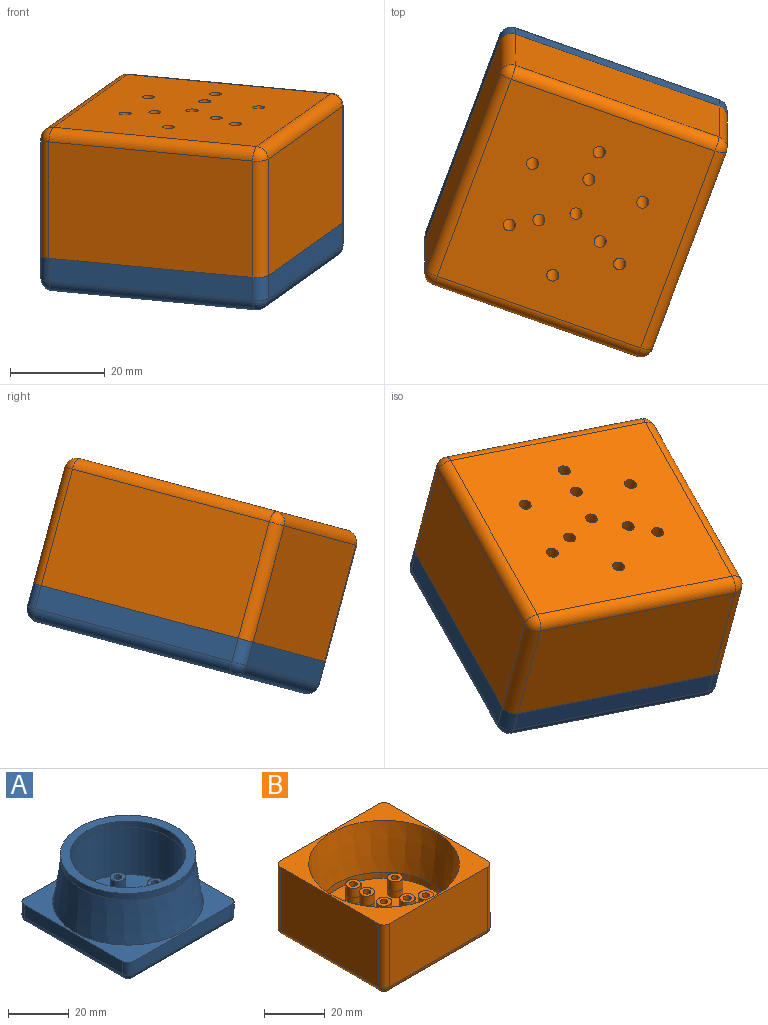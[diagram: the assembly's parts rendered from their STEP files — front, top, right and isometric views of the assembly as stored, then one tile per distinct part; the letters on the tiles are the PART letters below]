
ASSEMBLY  parts=2 mates=1
PART A: 52 faces, bbox 50.8x50.8x26.7 mm
  f0: plane 45.72x5.08mm, normal (-1,0,0), area 232.3mm2, adj f13,f17,f19,f51
  f1: plane 45.72x5.08mm, normal (0,-1,0), area 232.3mm2, adj f10,f16,f19,f51
  f2: plane 45.72x5.08mm, normal (1,0,0), area 232.3mm2, adj f8,f10,f11,f51
  f3: plane 45.72x5.08mm, normal (0,1,0), area 232.3mm2, adj f8,f12,f13,f51
  f4: plane 45.72x45.72mm, normal (0,0,-1), area 2044.9mm2, adj f11,f12,f16,f17,f38,f39,f40,f41
  f5: plane 38.09x38.09mm, normal (0,0,1), area 956.1mm2, adj f6,f20,f22,f24,f26,f28,f30,f32
  f6: cylinder r=19.04mm len=38.09mm, axis (0,0,-1), area 2279.4mm2, adj f5,f48
  f7: cone r=22.23mm half-angle=7.6deg, axis (0,0,-1), area 2837.1mm2, adj f47,f50
  f8: cylinder r=2.54mm len=5.08mm, axis (0,0,1), area 20.3mm2, adj f2,f3,f9,f51
  f9: sphere r=2.54mm, area 10.1mm2, adj f8,f11,f12
  f10: cylinder r=2.54mm len=5.08mm, axis (0,0,-1), area 20.3mm2, adj f1,f2,f14,f51
  f11: cylinder r=2.54mm len=45.72mm, axis (0,1,0), area 182.4mm2, adj f2,f4,f9,f14
  f12: cylinder r=2.54mm len=45.72mm, axis (-1,0,0), area 182.4mm2, adj f3,f4,f9,f15
  f13: cylinder r=2.54mm len=5.08mm, axis (0,0,1), area 20.3mm2, adj f0,f3,f15,f51
  f14: sphere r=2.54mm, area 10.1mm2, adj f10,f11,f16
  f15: sphere r=2.54mm, area 10.1mm2, adj f12,f13,f17
  f16: cylinder r=2.54mm len=45.72mm, axis (1,0,0), area 182.4mm2, adj f1,f4,f14,f18
  f17: cylinder r=2.54mm len=45.72mm, axis (0,-1,0), area 182.4mm2, adj f0,f4,f15,f18
  f18: sphere r=2.54mm, area 10.1mm2, adj f16,f17,f19
  f19: cylinder r=2.54mm len=5.08mm, axis (0,0,-1), area 20.3mm2, adj f0,f1,f18,f51
  f20: cylinder r=2.55mm len=5.09mm, axis (0,0,-1), area 60.9mm2, adj f5,f21
  f21: plane 5.09x5.09mm, normal (0,0,1), area 15.3mm2, adj f20,f39
  f22: cylinder r=2.55mm len=5.09mm, axis (0,0,-1), area 60.9mm2, adj f5,f23
  f23: plane 5.09x5.09mm, normal (0,0,1), area 15.3mm2, adj f22,f46
  f24: cylinder r=2.55mm len=5.09mm, axis (0,0,-1), area 60.9mm2, adj f5,f25
  f25: plane 5.09x5.09mm, normal (0,0,1), area 15.3mm2, adj f24,f45
  f26: cylinder r=2.55mm len=5.09mm, axis (0,0,-1), area 60.9mm2, adj f5,f27
  f27: plane 5.09x5.09mm, normal (0,0,1), area 15.3mm2, adj f26,f43
  f28: cylinder r=2.55mm len=5.09mm, axis (0,0,-1), area 60.9mm2, adj f5,f29
  f29: plane 5.09x5.09mm, normal (0,0,1), area 15.3mm2, adj f28,f42
  f30: cylinder r=2.55mm len=5.09mm, axis (0,0,-1), area 60.9mm2, adj f5,f31
  f31: plane 5.09x5.09mm, normal (0,0,1), area 15.3mm2, adj f30,f40
  f32: cylinder r=2.55mm len=5.09mm, axis (0,0,-1), area 60.9mm2, adj f5,f33
  f33: plane 5.09x5.09mm, normal (0,0,1), area 15.3mm2, adj f32,f41
  f34: cylinder r=2.55mm len=5.09mm, axis (0,0,-1), area 60.9mm2, adj f5,f35
  f35: plane 5.09x5.09mm, normal (0,0,1), area 15.3mm2, adj f34,f38
  f36: cylinder r=2.55mm len=5.09mm, axis (0,0,-1), area 60.9mm2, adj f5,f37
  f37: plane 5.09x5.09mm, normal (0,0,1), area 15.3mm2, adj f36,f44
  f38: cylinder r=1.27mm len=8.89mm, axis (0,0,1), area 70.9mm2, adj f4,f35
  f39: cylinder r=1.27mm len=8.89mm, axis (0,0,1), area 70.9mm2, adj f4,f21
  f40: cylinder r=1.27mm len=8.89mm, axis (0,0,1), area 70.9mm2, adj f4,f31
  f41: cylinder r=1.27mm len=8.89mm, axis (0,0,1), area 70.9mm2, adj f4,f33
  f42: cylinder r=1.27mm len=8.89mm, axis (0,0,1), area 70.9mm2, adj f4,f29
  f43: cylinder r=1.27mm len=8.89mm, axis (0,0,1), area 70.9mm2, adj f4,f27
  f44: cylinder r=1.27mm len=8.89mm, axis (0,0,1), area 70.9mm2, adj f4,f37
  f45: cylinder r=1.27mm len=8.89mm, axis (0,0,1), area 70.9mm2, adj f4,f25
  f46: cylinder r=1.27mm len=8.89mm, axis (0,0,1), area 70.9mm2, adj f4,f23
  f47: cone r=22.23mm half-angle=1.1deg, axis (0,0,1), area 355.2mm2, adj f7,f49
  f48: cone r=19.04mm half-angle=1.1deg, axis (0,0,-1), area 303.6mm2, adj f6,f49
  f49: plane 44.55x44.55mm, normal (0,0,1), area 425.1mm2, adj f47,f48
  f50: cylinder r=24.77mm len=49.53mm, axis (0,0,-1), area 395.2mm2, adj f7,f51
  f51: plane 50.8x50.8mm, normal (0,0,1), area 648.5mm2, adj f0,f1,f2,f3,f8,f10,f13,f19
PART B: 61 faces, bbox 50.8x50.8x27.9 mm
  f0: plane 45.72x25.4mm, normal (-1,0,0), area 1161.4mm2, adj f4,f49,f50,f51
  f1: plane 45.72x25.4mm, normal (0,-1,0), area 1161.3mm2, adj f4,f49,f54,f55
  f2: plane 45.72x25.4mm, normal (1,0,0), area 1161.4mm2, adj f4,f55,f56,f60
  f3: plane 45.72x25.4mm, normal (0,1,0), area 1161.3mm2, adj f4,f50,f56,f57
  f4: plane 50.8x50.8mm, normal (0,0,1), area 648.6mm2, adj f0,f1,f2,f3,f5,f49,f50,f55
  f5: cone r=22.25mm half-angle=7.5deg, axis (0,0,1), area 2838.1mm2, adj f4,f45
  f6: cylinder r=2.55mm len=5.09mm, axis (0,0,-1), area 60.9mm2, adj f7,f44
  f7: plane 5.09x5.09mm, normal (0,0,1), area 15.3mm2, adj f6,f26
  f8: cylinder r=2.55mm len=5.09mm, axis (0,0,-1), area 60.9mm2, adj f9,f43
  f9: plane 5.09x5.09mm, normal (0,0,1), area 15.3mm2, adj f8,f27
  f10: cylinder r=2.55mm len=5.09mm, axis (0,0,-1), area 60.9mm2, adj f11,f42
  f11: plane 5.09x5.09mm, normal (0,0,1), area 15.3mm2, adj f10,f33
  f12: cylinder r=2.55mm len=5.09mm, axis (0,0,-1), area 60.9mm2, adj f13,f41
  f13: plane 5.09x5.09mm, normal (0,0,1), area 15.3mm2, adj f12,f30
  f14: cylinder r=2.55mm len=5.09mm, axis (0,0,-1), area 60.9mm2, adj f15,f40
  f15: plane 5.09x5.09mm, normal (0,0,1), area 15.3mm2, adj f14,f28
  f16: cylinder r=2.55mm len=5.09mm, axis (0,0,-1), area 60.9mm2, adj f17,f39
  f17: plane 5.09x5.09mm, normal (0,0,1), area 15.3mm2, adj f16,f29
  f18: cylinder r=2.55mm len=5.09mm, axis (0,0,-1), area 60.9mm2, adj f19,f38
  f19: plane 5.09x5.09mm, normal (0,0,1), area 15.3mm2, adj f18,f31
  f20: cylinder r=2.55mm len=5.09mm, axis (0,0,-1), area 60.9mm2, adj f21,f37
  f21: plane 5.09x5.09mm, normal (0,0,1), area 15.3mm2, adj f20,f32
  f22: cylinder r=2.55mm len=5.09mm, axis (0,0,-1), area 60.9mm2, adj f23,f36
  f23: plane 5.09x5.09mm, normal (0,0,1), area 15.3mm2, adj f22,f34
  f24: cylinder r=2.55mm len=5.09mm, axis (0,0,-1), area 60.9mm2, adj f25,f46
  f25: plane 5.09x5.09mm, normal (0,0,1), area 15.3mm2, adj f24,f35
  f26: cylinder r=1.27mm len=12.7mm, axis (0,0,1), area 101.3mm2, adj f7,f48
  f27: cylinder r=1.27mm len=12.7mm, axis (0,0,1), area 101.3mm2, adj f9,f48
  f28: cylinder r=1.27mm len=12.7mm, axis (0,0,1), area 101.3mm2, adj f15,f48
  f29: cylinder r=1.27mm len=12.7mm, axis (0,0,1), area 101.3mm2, adj f17,f48
  f30: cylinder r=1.27mm len=12.7mm, axis (0,0,1), area 101.3mm2, adj f13,f48
  f31: cylinder r=1.27mm len=12.7mm, axis (0,0,1), area 101.3mm2, adj f19,f48
  f32: cylinder r=1.27mm len=12.7mm, axis (0,0,1), area 101.3mm2, adj f21,f48
  f33: cylinder r=1.27mm len=12.7mm, axis (0,0,1), area 101.3mm2, adj f11,f48
  f34: cylinder r=1.27mm len=12.7mm, axis (0,0,1), area 101.3mm2, adj f23,f48
  f35: cylinder r=1.27mm len=12.7mm, axis (0,0,1), area 101.3mm2, adj f25,f48
  f36: cone r=2.55mm half-angle=1deg, axis (0,0,1), area 40.3mm2, adj f22,f47
  f37: cone r=2.55mm half-angle=1deg, axis (0,0,1), area 40.3mm2, adj f20,f47
  f38: cone r=2.55mm half-angle=1deg, axis (0,0,1), area 40.3mm2, adj f18,f47
  f39: cone r=2.55mm half-angle=1deg, axis (0,0,1), area 40.3mm2, adj f16,f47
  f40: cone r=2.55mm half-angle=1deg, axis (0,0,1), area 40.3mm2, adj f14,f47
  f41: cone r=2.55mm half-angle=1deg, axis (0,0,1), area 40.3mm2, adj f12,f47
  f42: cone r=2.55mm half-angle=1deg, axis (0,0,1), area 40.3mm2, adj f10,f47
  f43: cone r=2.55mm half-angle=1deg, axis (0,0,1), area 40.3mm2, adj f8,f47
  f44: cone r=2.55mm half-angle=1deg, axis (0,0,1), area 40.3mm2, adj f6,f47
  f45: cone r=22.25mm half-angle=1deg, axis (0,0,-1), area 355.5mm2, adj f5,f47
  f46: cone r=2.55mm half-angle=1deg, axis (0,0,1), area 40.3mm2, adj f24,f47
  f47: plane 44.59x44.59mm, normal (0,0,1), area 1364.9mm2, adj f36,f37,f38,f39,f40,f41,f42,f43
  f48: plane 45.72x45.72mm, normal (0,0,-1), area 2039.8mm2, adj f26,f27,f28,f29,f30,f31,f32,f33
  f49: cylinder r=2.54mm len=25.4mm, axis (0,0,-1), area 101.3mm2, adj f0,f1,f4,f52
  f50: cylinder r=2.54mm len=25.4mm, axis (0,0,1), area 101.3mm2, adj f0,f3,f4,f53
  f51: cylinder r=2.54mm len=45.72mm, axis (0,-1,0), area 182.4mm2, adj f0,f48,f52,f53
  f52: sphere r=2.54mm, area 10.1mm2, adj f49,f51,f54
  f53: sphere r=2.54mm, area 10.1mm2, adj f50,f51,f57
  f54: cylinder r=2.54mm len=45.72mm, axis (1,0,0), area 182.4mm2, adj f1,f48,f52,f58
  f55: cylinder r=2.54mm len=25.4mm, axis (0,0,-1), area 101.3mm2, adj f1,f2,f4,f58
  f56: cylinder r=2.54mm len=25.4mm, axis (0,0,1), area 101.3mm2, adj f2,f3,f4,f59
  f57: cylinder r=2.54mm len=45.72mm, axis (-1,0,0), area 182.4mm2, adj f3,f48,f53,f59
  f58: sphere r=2.54mm, area 10.1mm2, adj f54,f55,f60
  f59: sphere r=2.54mm, area 10.1mm2, adj f56,f57,f60
  f60: cylinder r=2.54mm len=45.72mm, axis (0,1,0), area 182.4mm2, adj f2,f48,f58,f59
PLACE A rot(axis=(0.59,0.1,-0.8),25deg) t=(-73.2,43.22,3.29)mm
PLACE B rot(axis=(-0.17,-0.98,-0.13),177.4deg) t=(-48.33,95.25,54.04)mm
MATE revolute A.f6 <-> B.f5  axis (0,-0.26,0.97) through (-72.41,36.04,28.97)mm
